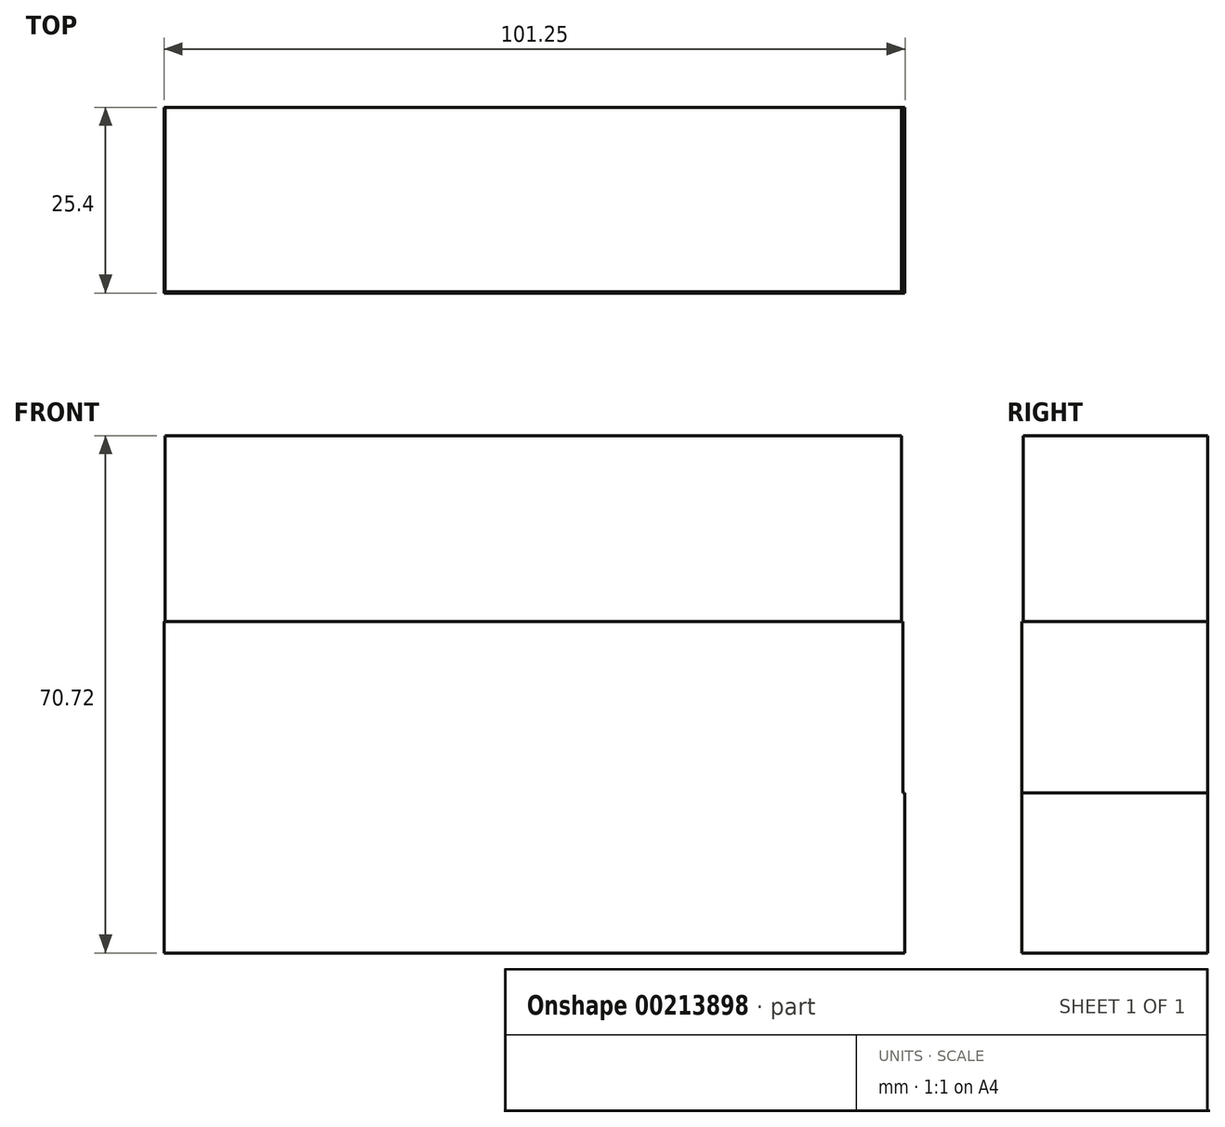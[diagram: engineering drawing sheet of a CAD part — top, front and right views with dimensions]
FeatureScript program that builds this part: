
annotation { "Feature Type Name" : "Feature", "Feature Type Description" : "" }
export const myFeature = defineFeature(function(context is Context, id is Id, definition is map)
    precondition{}
    {
        {
            var Q0;
            Q0=qCreatedBy(makeId("Front.planeOp"),FACE);
            var sketch = newSketch(context, id + "F0", { "sketchPlane" : qUnion([Q0])});
            skArc(sketch, "E0", {"start": v(45.15, 0) * mm, "mid": v(-4.97, 38.84) * mm, "end": v(-55.08, 0) * mm});
            skSolve(sketch);
        }
        {
            var Q0;
            Q0=sQuery(id+"F0.wireOp",EDGE,"E0");
            extrude(context, id + "F1", {"bodyType" : ToolBodyType.SURFACE, "surfaceEntities" : qUnion([Q0]), "depth" : 25.4 * mm});
        }
        {
            var Q0;
            Q0=qCreatedBy(makeId("Top.planeOp"),FACE);
            var sketch = newSketch(context, id + "F2", { "sketchPlane" : qUnion([Q0])});
            skLineSegment(sketch, "E1.bottom", {"start": v(-55.54, 0) * mm, "end": v(45.1, 0) * mm});
            skLineSegment(sketch, "E1.top", {"start": v(-55.54, -25.23) * mm, "end": v(45.1, -25.23) * mm});
            skLineSegment(sketch, "E1.left", {"start": v(-55.54, 0) * mm, "end": v(-55.54, -25.23) * mm});
            skLineSegment(sketch, "E1.right", {"start": v(45.1, 0) * mm, "end": v(45.1, -25.23) * mm});
            skSolve(sketch);
        }
        {
            var Q0;
            Q0=makeQuery(id+"F2.imprint","IMPRINT",FACE,{"disambiguationData":[TD([[makeQuery(id+"F2.imprint","IMPRINT",EDGE,{"derivedFrom":sQuery(id+"F2.wireOp",EDGE,"E1.bottom")}),-1.0]])]});
            extrude(context, id + "F3", {"entities" : qUnion([Q0]), "depth" : 25.4 * mm});
        }
        {
            var Q0;
            Q0=qCreatedBy(makeId("Front.planeOp"),FACE);
            var sketch = newSketch(context, id + "F4", { "sketchPlane" : qUnion([Q0])});
            skLineSegment(sketch, "E2.bottom", {"start": v(-55.7, 0) * mm, "end": v(45.28, 0) * mm});
            skLineSegment(sketch, "E2.top", {"start": v(-55.7, -23.42) * mm, "end": v(45.28, -23.42) * mm});
            skLineSegment(sketch, "E2.left", {"start": v(-55.7, 0) * mm, "end": v(-55.7, -23.42) * mm});
            skLineSegment(sketch, "E2.right", {"start": v(45.28, 0) * mm, "end": v(45.28, -23.42) * mm});
            skSolve(sketch);
        }
        {
            var Q0;
            Q0=makeQuery(id+"F4.imprint","IMPRINT",FACE,{"disambiguationData":[TD([[makeQuery(id+"F4.imprint","IMPRINT",EDGE,{"derivedFrom":sQuery(id+"F4.wireOp",EDGE,"E2.bottom")}),-1.0]])]});
            extrude(context, id + "F5", {"entities" : qUnion([Q0]), "operationType" : NewBodyOperationType.ADD, "depth" : 25.4 * mm});
        }
        {
            var Q0;
            Q0=qCreatedBy(makeId("Front.planeOp"),FACE);
            var sketch = newSketch(context, id + "F6", { "sketchPlane" : qUnion([Q0])});
            skArc(sketch, "E3", {"start": v(-55.7, -22.88) * mm, "mid": v(-5.61, -57.65) * mm, "end": v(45.01, -23.69) * mm});
            skSolve(sketch);
        }
        {
            var Q0;
            Q0=sQuery(id+"F6.wireOp",EDGE,"E3");
            extrude(context, id + "F7", {"bodyType" : ToolBodyType.SURFACE, "surfaceEntities" : qUnion([Q0]), "depth" : 25.4 * mm});
        }
        {
            var Q0;
            Q0=qCreatedBy(makeId("Front.planeOp"),FACE);
            var sketch = newSketch(context, id + "F8", { "sketchPlane" : qUnion([Q0])});
            skLineSegment(sketch, "E4.bottom", {"start": v(-55.7, -23.42) * mm, "end": v(45.55, -23.42) * mm});
            skLineSegment(sketch, "E4.top", {"start": v(-55.7, -45.32) * mm, "end": v(45.55, -45.32) * mm});
            skLineSegment(sketch, "E4.left", {"start": v(-55.7, -23.42) * mm, "end": v(-55.7, -45.32) * mm});
            skLineSegment(sketch, "E4.right", {"start": v(45.55, -23.42) * mm, "end": v(45.55, -45.32) * mm});
            skSolve(sketch);
        }
        {
            var Q0;
            Q0=makeQuery(id+"F8.imprint","IMPRINT",FACE,{"disambiguationData":[TD([[makeQuery(id+"F8.imprint","IMPRINT",EDGE,{"derivedFrom":sQuery(id+"F8.wireOp",EDGE,"E4.bottom")}),-1.0]])]});
            extrude(context, id + "F9", {"entities" : qUnion([Q0]), "operationType" : NewBodyOperationType.ADD, "depth" : 25.4 * mm});
        }
    });
